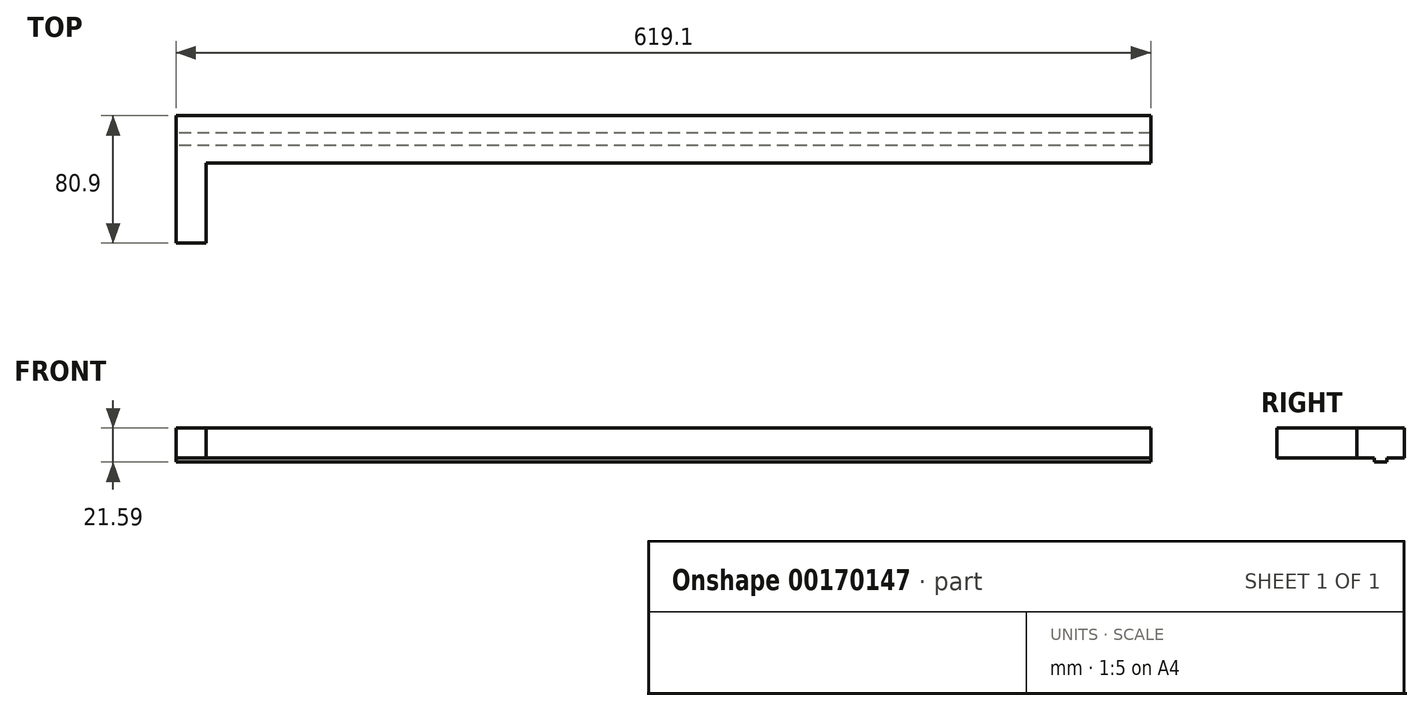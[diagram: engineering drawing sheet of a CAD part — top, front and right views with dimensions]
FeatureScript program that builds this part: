
annotation { "Feature Type Name" : "Feature", "Feature Type Description" : "" }
export const myFeature = defineFeature(function(context is Context, id is Id, definition is map)
    precondition{}
    {
        {
            var Q0;
            Q0=qCreatedBy(makeId("Right.planeOp"),FACE);
            var sketch = newSketch(context, id + "F0", { "sketchPlane" : qUnion([Q0])});
            skLineSegment(sketch, "E0.bottom", {"start": v(-15.05, 19.05) * mm, "end": v(15.05, 19.05) * mm});
            skLineSegment(sketch, "E0.top", {"start": v(-15.05, 0) * mm, "end": v(-4, 0) * mm});
            skLineSegment(sketch, "E0.left", {"start": v(-15.05, 19.05) * mm, "end": v(-15.05, 0) * mm});
            skLineSegment(sketch, "E0.right", {"start": v(15.05, 19.05) * mm, "end": v(15.05, 0) * mm});
            skLineSegment(sketch, "E1", {"start": v(-4, 0) * mm, "end": v(-4, -2.54) * mm});
            skLineSegment(sketch, "E2", {"start": v(-4, -2.54) * mm, "end": v(4, -2.54) * mm});
            skLineSegment(sketch, "E3", {"start": v(4, -2.54) * mm, "end": v(4, 0) * mm});
            skLineSegment(sketch, "E4.trimOffspring", {"start": v(4, 0) * mm, "end": v(15.05, 0) * mm});
            skSolve(sketch);
        }
        {
            var Q0;
            Q0=qCreatedBy(makeId("Top.planeOp"),FACE);
            cPlane(context, id + "F1", {"entities" : qUnion([Q0]), "cplaneType" : CPlaneType.OFFSET, "offset" : 19.05 * mm, "width" : 152.4 * mm, "height" : 152.4 * mm});
        }
        {
            var Q0;
            Q0=qCreatedBy(id+"F1.planeOp",FACE);
            var sketch = newSketch(context, id + "F2", { "sketchPlane" : qUnion([Q0])});
            skLineSegment(sketch, "E5", {"start": v(0, 0) * mm, "end": v(-619.1, 0) * mm});
            skLineSegment(sketch, "E6", {"start": v(-619.1, 0) * mm, "end": v(-619.1, -65.85) * mm});
            skSolve(sketch);
        }
        {
            var Q0;
            Q0=makeQuery(id+"F0.imprint","IMPRINT",FACE,{"disambiguationData":[TD([[makeQuery(id+"F0.imprint","IMPRINT",EDGE,{"derivedFrom":sQuery(id+"F0.wireOp",EDGE,"E0.bottom")}),-1.0]])]});
            var Q1;
            Q1=sQuery(id+"F2.wireOp",EDGE,"E5");
            sweep(context, id + "F3", {"profiles" : qUnion([Q0]), "path" : qUnion([Q1])});
        }
        {
            var Q0;
            Q0=makeQuery(id+"F3.opSweep","SWEPT_FACE",FACE,{"disambiguationData":[OSD([sQuery(id+"F0.wireOp",EDGE,"E0.left"),sQuery(id+"F2.wireOp",EDGE,"E5")])]});
            var sketch = newSketch(context, id + "F4", { "sketchPlane" : qUnion([Q0])});
            skLineSegment(sketch, "E7", {"start": v(-619.1, 19.05) * mm, "end": v(-619.1, 0) * mm});
            skLineSegment(sketch, "E8", {"start": v(-619.1, 0) * mm, "end": v(-600.05, 0) * mm});
            skLineSegment(sketch, "E9", {"start": v(-600.05, 0) * mm, "end": v(-600.05, 19.05) * mm});
            skLineSegment(sketch, "E10", {"start": v(-600.05, 19.05) * mm, "end": v(-619.1, 19.05) * mm});
            skSolve(sketch);
        }
        {
            var Q0;
            Q0=makeQuery(id+"F4.imprint","IMPRINT",FACE,{"disambiguationData":[TD([[makeQuery(id+"F4.imprint","IMPRINT",EDGE,{"derivedFrom":sQuery(id+"F4.wireOp",EDGE,"E7")}),-1.0]])]});
            extrude(context, id + "F5", {"entities" : qUnion([Q0]), "operationType" : NewBodyOperationType.ADD, "depth" : 50.8 * mm});
        }
    });
